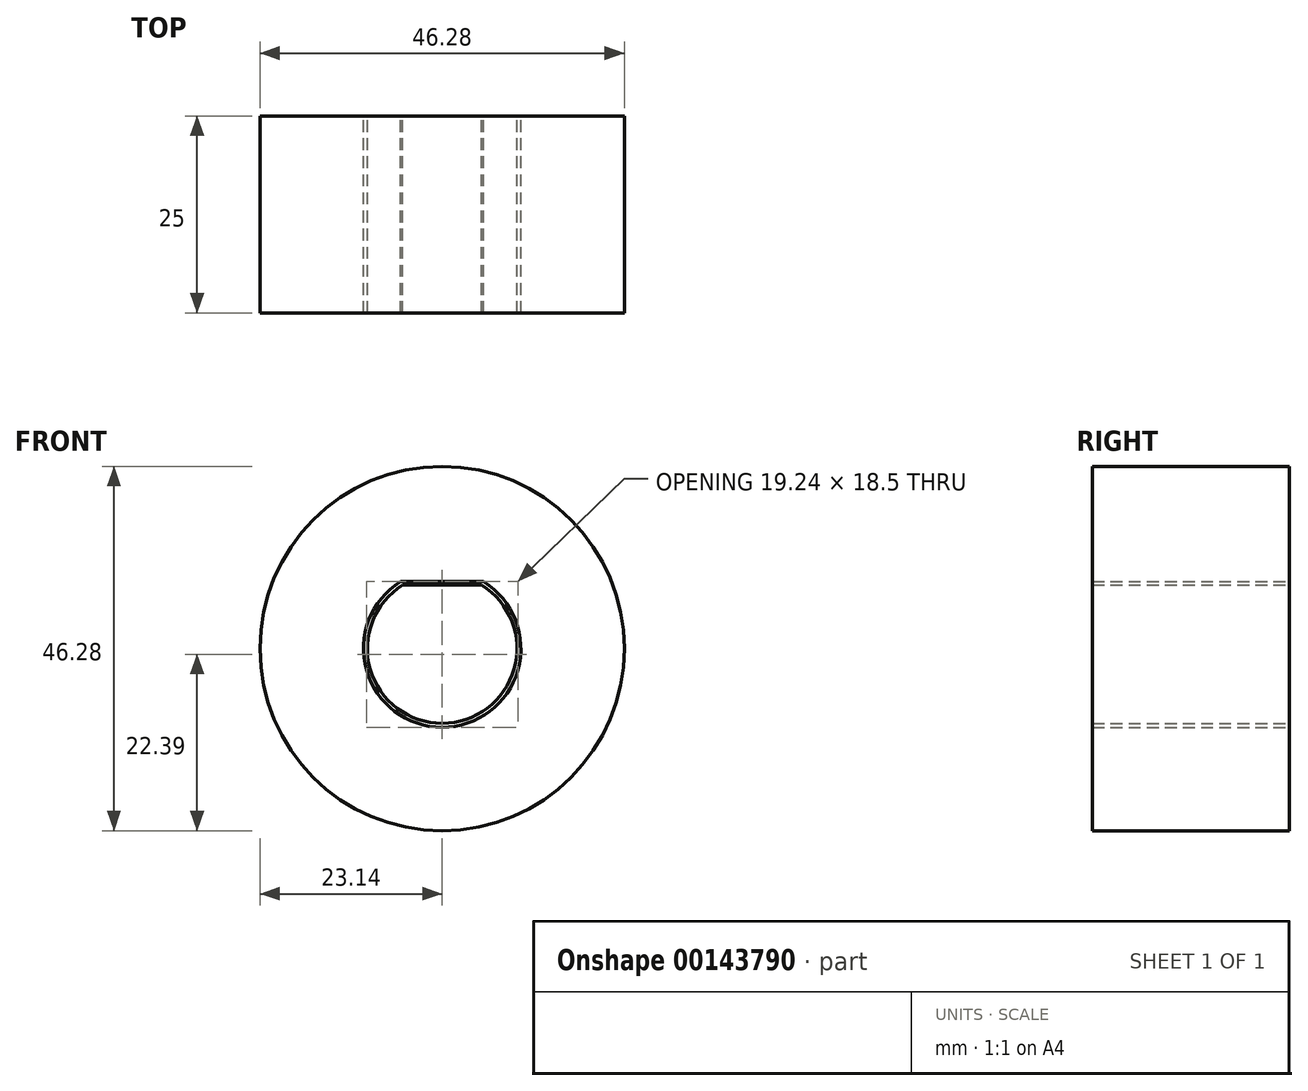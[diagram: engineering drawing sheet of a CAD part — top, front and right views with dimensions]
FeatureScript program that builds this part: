
annotation { "Feature Type Name" : "Feature", "Feature Type Description" : "" }
export const myFeature = defineFeature(function(context is Context, id is Id, definition is map)
    precondition{}
    {
        {
            var Q0;
            Q0=qCreatedBy(makeId("Front.planeOp"),FACE);
            var sketch = newSketch(context, id + "F0", { "sketchPlane" : qUnion([Q0])});
            skArc(sketch, "E0", {"start": v(-5.27, 8.5) * mm, "mid": v(0, -10) * mm, "end": v(5.27, 8.5) * mm});
            skCircle(sketch, "E1", {"center": v(0, 0) * mm, "radius": 23.14 * mm});
            skLineSegment(sketch, "E2", {"start": v(-5.27, 8.5) * mm, "end": v(5.27, 8.5) * mm});
            skSolve(sketch);
        }
        {
            var Q0;
            Q0 = qSketchRegion(id + "F0", true);
            extrude(context, id + "F1", {"entities" : qUnion([Q0]), "depth" : 25 * mm});
        }
        {
            var Q0;
            Q0=qCreatedBy(makeId("Front.planeOp"),FACE);
            var sketch = newSketch(context, id + "F2", { "sketchPlane" : qUnion([Q0])});
            skArc(sketch, "E3.0", {"start": v(-5, 8.07) * mm, "mid": v(0, -9.5) * mm, "end": v(5, 8.07) * mm});
            skLineSegment(sketch, "E4", {"start": v(-5, 8.07) * mm, "end": v(5, 8.07) * mm});
            skSolve(sketch);
        }
        {
            var Q0;
            Q0 = qSketchRegion(id + "F2", true);
            extrude(context, id + "F3", {"entities" : qUnion([Q0]), "depth" : 25 * mm});
        }
    });
